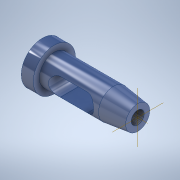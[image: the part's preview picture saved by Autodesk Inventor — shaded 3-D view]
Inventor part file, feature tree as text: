
AUTODESK INVENTOR PART (.ipt)
format: ipt  version: 2021.1 (Build 251245000, 245)  size: 147,968 bytes
history: native  units: in
note: dims shown in document units (in); Inventor stores cm internally (conversion verified against a paired STEP export)
features: sketch x3, revolve x1, extrude x1, hole x1
ambient origin geometry x8: Origin, YZ Plane, XZ Plane, XY Plane, X Axis, Y Axis, Z Axis, Center Point
bodies: Solid1 (feature_tree)
feature tree (6):
  revolve  "Revolution1"  [1 undecoded]
  extrude  "Extrusion1"  Depth=0.4724in
  hole  "Hole1"  [1 undecoded]
  sketch  "Sketch1"  dims[d0=0.4724in d1=2.3228in]
  sketch  "Sketch2"  dims[d2=0.9449in d3=0.4724in]
  sketch  "Sketch3"  dims[d4=0.8268in d5=0.5906in d6=90.0deg d7=1.063in d8=1.1811in d9=0.3543in d10=0.3937in d11=0.0in d12=0.5086in d13=1.378in d14=0.1575in d15=0.0787in d16=90.0deg d17=1.5748in d18=0.8108in]
note: 2 required parameter values undecoded (feature->parameter linkage not recoverable at this tier; creation-order binding heuristic only, values carry confidence <= 0.55)